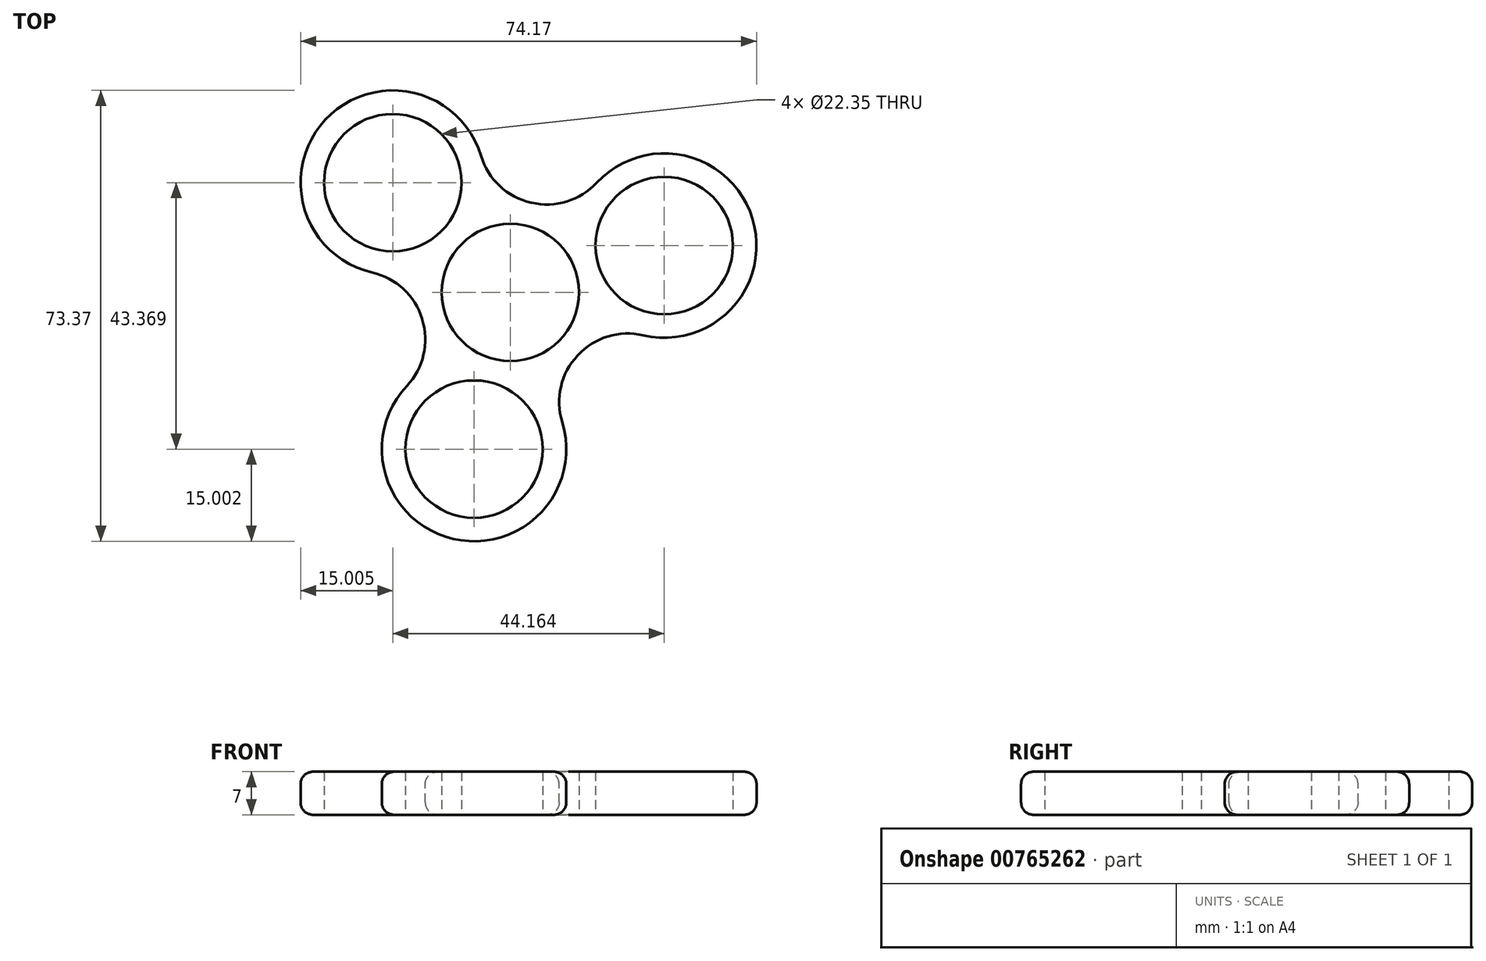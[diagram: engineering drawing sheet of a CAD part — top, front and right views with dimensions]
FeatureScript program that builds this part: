
annotation { "Feature Type Name" : "Feature", "Feature Type Description" : "" }
export const myFeature = defineFeature(function(context is Context, id is Id, definition is map)
    precondition{}
    {
        {
            var Q0;
            Q0=qCreatedBy(makeId("Top.planeOp"),FACE);
            var sketch = newSketch(context, id + "F0", { "sketchPlane" : qUnion([Q0])});
            skCircle(sketch, "E0", {"center": v(0, 0) * mm, "radius": 11.18 * mm});
            skLineSegment(sketch, "E1", {"start": v(0, 0) * mm, "end": v(-19.13, 17.87) * mm});
            skLineSegment(sketch, "E2", {"start": v(0, 0) * mm, "end": v(25.04, 7.63) * mm});
            skLineSegment(sketch, "E3", {"start": v(0, 0) * mm, "end": v(-5.91, -25.5) * mm});
            skCircle(sketch, "E4", {"center": v(-19.13, 17.87) * mm, "radius": 11.18 * mm});
            skCircle(sketch, "E5", {"center": v(25.04, 7.63) * mm, "radius": 11.18 * mm});
            skCircle(sketch, "E6", {"center": v(-5.91, -25.5) * mm, "radius": 11.18 * mm});
            skCircle(sketch, "E7", {"center": v(0, 0) * mm, "radius": 15 * mm});
            skCircle(sketch, "E8", {"center": v(-19.13, 17.87) * mm, "radius": 15 * mm});
            skCircle(sketch, "E9", {"center": v(25.04, 7.63) * mm, "radius": 15 * mm});
            skCircle(sketch, "E10", {"center": v(-5.91, -25.5) * mm, "radius": 15 * mm});
            skLineSegment(sketch, "E11", {"start": v(-19.13, 17.87) * mm, "end": v(-8.88, 28.83) * mm});
            skLineSegment(sketch, "E12", {"start": v(25.04, 7.63) * mm, "end": v(20.67, 21.98) * mm});
            skLineSegment(sketch, "E13", {"start": v(-5.91, -25.5) * mm, "end": v(8.7, -28.89) * mm});
            skLineSegment(sketch, "E14", {"start": v(-5.91, -25.5) * mm, "end": v(-20.53, -22.1) * mm});
            skLineSegment(sketch, "E15", {"start": v(-19.13, 17.87) * mm, "end": v(-29.37, 6.91) * mm});
            skLineSegment(sketch, "E16", {"start": v(25.04, 7.63) * mm, "end": v(29.41, -6.72) * mm});
            skArc(sketch, "E17", {"start": v(-8.88, 28.83) * mm, "mid": v(3.39, 14.61) * mm, "end": v(20.67, 21.98) * mm});
            skArc(sketch, "E18", {"start": v(-20.53, -22.1) * mm, "mid": v(-14.35, -4.37) * mm, "end": v(-29.37, 6.91) * mm});
            skArc(sketch, "E19", {"start": v(29.41, -6.72) * mm, "mid": v(10.96, -10.24) * mm, "end": v(8.7, -28.89) * mm});
            skSolve(sketch);
        }
        {
            var Q0;
            {var subQ0=sQuery(id+"F0.wireOp",EDGE,"E15");var subQ1=sQuery(id+"F0.wireOp",EDGE,"E4");var subQ2=makeQuery(id+"F0.imprint","INTERSECT",VERTEX,{"derivedFrom":[subQ1,subQ0]});Q0=makeQuery(id+"F0.imprint","IMPRINT",FACE,{"disambiguationData":[TD([[makeQuery(id+"F0.imprint","IMPRINT",EDGE,{"disambiguationData":[TD([[subQ2,1.0]])],"derivedFrom":subQ1}),-1.0]])]});}
            var Q1;
            {var subQ0=sQuery(id+"F0.wireOp",EDGE,"E17");var subQ1=sQuery(id+"F0.wireOp",EDGE,"E8");var subQ3=makeQuery(id+"F0.imprint","INTERSECT",VERTEX,{"derivedFrom":[subQ1,subQ0]});Q1=makeQuery(id+"F0.imprint","IMPRINT",FACE,{"disambiguationData":[TD([[makeQuery(id+"F0.imprint","IMPRINT",EDGE,{"disambiguationData":[TD([[subQ3,-1.0]])],"derivedFrom":subQ1}),1.0]])]});}
            var Q2;
            {var subQ0=sQuery(id+"F0.wireOp",EDGE,"E17");var subQ2=sQuery(id+"F0.wireOp",EDGE,"E8");var subQ6=makeQuery(id+"F0.imprint","INTERSECT",VERTEX,{"derivedFrom":[subQ2,subQ0]});Q2=makeQuery(id+"F0.imprint","IMPRINT",FACE,{"disambiguationData":[TD([[makeQuery(id+"F0.imprint","IMPRINT",EDGE,{"disambiguationData":[TD([[subQ6,1.0]])],"derivedFrom":subQ2}),1.0]])]});}
            var Q3;
            {var subQ0=sQuery(id+"F0.wireOp",EDGE,"E8");var subQ3=sQuery(id+"F0.wireOp",EDGE,"E7");var subQ5=makeQuery(id+"F0.imprint","INTERSECT",VERTEX,{"disambiguationData":[OD(0.0)],"derivedFrom":[subQ3,subQ0]});Q3=makeQuery(id+"F0.imprint","IMPRINT",FACE,{"disambiguationData":[TD([[makeQuery(id+"F0.imprint","IMPRINT",EDGE,{"disambiguationData":[TD([[subQ5,-1.0]])],"derivedFrom":subQ3}),1.0]])]});}
            var Q4;
            {var subQ0=sQuery(id+"F0.wireOp",EDGE,"E8");var subQ3=sQuery(id+"F0.wireOp",EDGE,"E7");var subQ5=makeQuery(id+"F0.imprint","INTERSECT",VERTEX,{"disambiguationData":[OD(1.0)],"derivedFrom":[subQ3,subQ0]});Q4=makeQuery(id+"F0.imprint","IMPRINT",FACE,{"disambiguationData":[TD([[makeQuery(id+"F0.imprint","IMPRINT",EDGE,{"disambiguationData":[TD([[subQ5,1.0]])],"derivedFrom":subQ3}),1.0]])]});}
            var Q5;
            {var subQ0=sQuery(id+"F0.wireOp",EDGE,"E18");var subQ1=sQuery(id+"F0.wireOp",EDGE,"E8");var subQ2=makeQuery(id+"F0.imprint","INTERSECT",VERTEX,{"derivedFrom":[subQ1,subQ0]});Q5=makeQuery(id+"F0.imprint","IMPRINT",FACE,{"disambiguationData":[TD([[makeQuery(id+"F0.imprint","IMPRINT",EDGE,{"disambiguationData":[TD([[subQ2,-1.0]])],"derivedFrom":subQ1}),1.0]])]});}
            var Q6;
            {var subQ0=sQuery(id+"F0.wireOp",EDGE,"E18");var subQ1=sQuery(id+"F0.wireOp",EDGE,"E8");var subQ3=makeQuery(id+"F0.imprint","INTERSECT",VERTEX,{"derivedFrom":[subQ1,subQ0]});Q6=makeQuery(id+"F0.imprint","IMPRINT",FACE,{"disambiguationData":[TD([[makeQuery(id+"F0.imprint","IMPRINT",EDGE,{"disambiguationData":[TD([[subQ3,1.0]])],"derivedFrom":subQ1}),1.0]])]});}
            var Q7;
            {var subQ0=sQuery(id+"F0.wireOp",EDGE,"E18");var subQ1=sQuery(id+"F0.wireOp",EDGE,"E10");var subQ3=makeQuery(id+"F0.imprint","INTERSECT",VERTEX,{"derivedFrom":[subQ1,subQ0]});Q7=makeQuery(id+"F0.imprint","IMPRINT",FACE,{"disambiguationData":[TD([[makeQuery(id+"F0.imprint","IMPRINT",EDGE,{"disambiguationData":[TD([[subQ3,-1.0]])],"derivedFrom":subQ1}),1.0]])]});}
            var Q8;
            {var subQ0=sQuery(id+"F0.wireOp",EDGE,"E18");var subQ2=sQuery(id+"F0.wireOp",EDGE,"E10");var subQ6=makeQuery(id+"F0.imprint","INTERSECT",VERTEX,{"derivedFrom":[subQ2,subQ0]});Q8=makeQuery(id+"F0.imprint","IMPRINT",FACE,{"disambiguationData":[TD([[makeQuery(id+"F0.imprint","IMPRINT",EDGE,{"disambiguationData":[TD([[subQ6,1.0]])],"derivedFrom":subQ2}),1.0]])]});}
            var Q9;
            {var subQ0=sQuery(id+"F0.wireOp",EDGE,"E10");var subQ3=sQuery(id+"F0.wireOp",EDGE,"E7");var subQ5=makeQuery(id+"F0.imprint","INTERSECT",VERTEX,{"disambiguationData":[OD(0.0)],"derivedFrom":[subQ3,subQ0]});Q9=makeQuery(id+"F0.imprint","IMPRINT",FACE,{"disambiguationData":[TD([[makeQuery(id+"F0.imprint","IMPRINT",EDGE,{"disambiguationData":[TD([[subQ5,-1.0]])],"derivedFrom":subQ3}),1.0]])]});}
            var Q10;
            {var subQ0=sQuery(id+"F0.wireOp",EDGE,"E10");var subQ3=sQuery(id+"F0.wireOp",EDGE,"E7");var subQ5=makeQuery(id+"F0.imprint","INTERSECT",VERTEX,{"disambiguationData":[OD(1.0)],"derivedFrom":[subQ3,subQ0]});Q10=makeQuery(id+"F0.imprint","IMPRINT",FACE,{"disambiguationData":[TD([[makeQuery(id+"F0.imprint","IMPRINT",EDGE,{"disambiguationData":[TD([[subQ5,1.0]])],"derivedFrom":subQ3}),1.0]])]});}
            var Q11;
            {var subQ0=sQuery(id+"F0.wireOp",EDGE,"E19");var subQ1=sQuery(id+"F0.wireOp",EDGE,"E10");var subQ3=makeQuery(id+"F0.imprint","INTERSECT",VERTEX,{"derivedFrom":[subQ1,subQ0]});Q11=makeQuery(id+"F0.imprint","IMPRINT",FACE,{"disambiguationData":[TD([[makeQuery(id+"F0.imprint","IMPRINT",EDGE,{"disambiguationData":[TD([[subQ3,1.0]])],"derivedFrom":subQ1}),1.0]])]});}
            var Q12;
            {var subQ0=sQuery(id+"F0.wireOp",EDGE,"E19");var subQ1=sQuery(id+"F0.wireOp",EDGE,"E10");var subQ2=makeQuery(id+"F0.imprint","INTERSECT",VERTEX,{"derivedFrom":[subQ1,subQ0]});Q12=makeQuery(id+"F0.imprint","IMPRINT",FACE,{"disambiguationData":[TD([[makeQuery(id+"F0.imprint","IMPRINT",EDGE,{"disambiguationData":[TD([[subQ2,-1.0]])],"derivedFrom":subQ1}),1.0]])]});}
            var Q13;
            {var subQ0=sQuery(id+"F0.wireOp",EDGE,"E14");var subQ1=sQuery(id+"F0.wireOp",EDGE,"E6");var subQ2=makeQuery(id+"F0.imprint","INTERSECT",VERTEX,{"derivedFrom":[subQ1,subQ0]});Q13=makeQuery(id+"F0.imprint","IMPRINT",FACE,{"disambiguationData":[TD([[makeQuery(id+"F0.imprint","IMPRINT",EDGE,{"disambiguationData":[TD([[subQ2,-1.0]])],"derivedFrom":subQ1}),-1.0]])]});}
            var Q14;
            {var subQ1=sQuery(id+"F0.wireOp",EDGE,"E7");var subQ5=makeQuery(id+"F0.imprint","INTERSECT",VERTEX,{"derivedFrom":[subQ1,sQuery(id+"F0.wireOp",EDGE,"E18")]});Q14=makeQuery(id+"F0.imprint","IMPRINT",FACE,{"disambiguationData":[TD([[makeQuery(id+"F0.imprint","IMPRINT",EDGE,{"disambiguationData":[TD([[subQ5,1.0]])],"derivedFrom":subQ1}),1.0]])]});}
            var Q15;
            {var subQ1=sQuery(id+"F0.wireOp",EDGE,"E7");var subQ5=makeQuery(id+"F0.imprint","INTERSECT",VERTEX,{"derivedFrom":[subQ1,sQuery(id+"F0.wireOp",EDGE,"E19")]});Q15=makeQuery(id+"F0.imprint","IMPRINT",FACE,{"disambiguationData":[TD([[makeQuery(id+"F0.imprint","IMPRINT",EDGE,{"disambiguationData":[TD([[subQ5,1.0]])],"derivedFrom":subQ1}),1.0]])]});}
            var Q16;
            {var subQ0=sQuery(id+"F0.wireOp",EDGE,"E9");var subQ3=sQuery(id+"F0.wireOp",EDGE,"E7");var subQ5=makeQuery(id+"F0.imprint","INTERSECT",VERTEX,{"disambiguationData":[OD(1.0)],"derivedFrom":[subQ3,subQ0]});Q16=makeQuery(id+"F0.imprint","IMPRINT",FACE,{"disambiguationData":[TD([[makeQuery(id+"F0.imprint","IMPRINT",EDGE,{"disambiguationData":[TD([[subQ5,-1.0]])],"derivedFrom":subQ3}),1.0]])]});}
            var Q17;
            {var subQ0=sQuery(id+"F0.wireOp",EDGE,"E9");var subQ3=sQuery(id+"F0.wireOp",EDGE,"E7");var subQ5=makeQuery(id+"F0.imprint","INTERSECT",VERTEX,{"disambiguationData":[OD(0.0)],"derivedFrom":[subQ3,subQ0]});Q17=makeQuery(id+"F0.imprint","IMPRINT",FACE,{"disambiguationData":[TD([[makeQuery(id+"F0.imprint","IMPRINT",EDGE,{"disambiguationData":[TD([[subQ5,1.0]])],"derivedFrom":subQ3}),1.0]])]});}
            var Q18;
            {var subQ1=sQuery(id+"F0.wireOp",EDGE,"E7");var subQ5=makeQuery(id+"F0.imprint","INTERSECT",VERTEX,{"derivedFrom":[subQ1,sQuery(id+"F0.wireOp",EDGE,"E17")]});Q18=makeQuery(id+"F0.imprint","IMPRINT",FACE,{"disambiguationData":[TD([[makeQuery(id+"F0.imprint","IMPRINT",EDGE,{"disambiguationData":[TD([[subQ5,1.0]])],"derivedFrom":subQ1}),1.0]])]});}
            var Q19;
            {var subQ0=sQuery(id+"F0.wireOp",EDGE,"E17");var subQ2=sQuery(id+"F0.wireOp",EDGE,"E9");var subQ6=makeQuery(id+"F0.imprint","INTERSECT",VERTEX,{"derivedFrom":[subQ2,subQ0]});Q19=makeQuery(id+"F0.imprint","IMPRINT",FACE,{"disambiguationData":[TD([[makeQuery(id+"F0.imprint","IMPRINT",EDGE,{"disambiguationData":[TD([[subQ6,-1.0]])],"derivedFrom":subQ2}),1.0]])]});}
            var Q20;
            {var subQ0=sQuery(id+"F0.wireOp",EDGE,"E17");var subQ1=sQuery(id+"F0.wireOp",EDGE,"E9");var subQ3=makeQuery(id+"F0.imprint","INTERSECT",VERTEX,{"derivedFrom":[subQ1,subQ0]});Q20=makeQuery(id+"F0.imprint","IMPRINT",FACE,{"disambiguationData":[TD([[makeQuery(id+"F0.imprint","IMPRINT",EDGE,{"disambiguationData":[TD([[subQ3,1.0]])],"derivedFrom":subQ1}),1.0]])]});}
            var Q21;
            {var subQ0=sQuery(id+"F0.wireOp",EDGE,"E12");var subQ1=sQuery(id+"F0.wireOp",EDGE,"E5");var subQ2=makeQuery(id+"F0.imprint","INTERSECT",VERTEX,{"derivedFrom":[subQ1,subQ0]});Q21=makeQuery(id+"F0.imprint","IMPRINT",FACE,{"disambiguationData":[TD([[makeQuery(id+"F0.imprint","IMPRINT",EDGE,{"disambiguationData":[TD([[subQ2,1.0]])],"derivedFrom":subQ1}),-1.0]])]});}
            var Q22;
            {var subQ0=sQuery(id+"F0.wireOp",EDGE,"E19");var subQ2=sQuery(id+"F0.wireOp",EDGE,"E9");var subQ9=makeQuery(id+"F0.imprint","INTERSECT",VERTEX,{"derivedFrom":[subQ2,subQ0]});Q22=makeQuery(id+"F0.imprint","IMPRINT",FACE,{"disambiguationData":[TD([[makeQuery(id+"F0.imprint","IMPRINT",EDGE,{"disambiguationData":[TD([[subQ9,1.0]])],"derivedFrom":subQ2}),1.0]])]});}
            var Q23;
            {var subQ0=sQuery(id+"F0.wireOp",EDGE,"E19");var subQ1=sQuery(id+"F0.wireOp",EDGE,"E9");var subQ3=makeQuery(id+"F0.imprint","INTERSECT",VERTEX,{"derivedFrom":[subQ1,subQ0]});Q23=makeQuery(id+"F0.imprint","IMPRINT",FACE,{"disambiguationData":[TD([[makeQuery(id+"F0.imprint","IMPRINT",EDGE,{"disambiguationData":[TD([[subQ3,-1.0]])],"derivedFrom":subQ1}),1.0]])]});}
            extrude(context, id + "F1", {"entities" : qUnion([Q0, Q1, Q2, Q3, Q4, Q5, Q6, Q7, Q8, Q9, Q10, Q11, Q12, Q13, Q14, Q15, Q16, Q17, Q18, Q19, Q20, Q21, Q22, Q23]), "depth" : 7 * mm, "offsetDistance" : 25 * mm});
        }
        {
            var Q0;
            {var subQ0=sQuery(id+"F0.wireOp",EDGE,"E8");var subQ1=sQuery(id+"F0.wireOp",EDGE,"E7");Q0=makeQuery(id+"F1.opExtrude","SWEPT_EDGE",EDGE,{"disambiguationData":[OSD([subQ1,subQ0]),TDD([makeQuery(id+"F0.imprint","INTERSECT",VERTEX,{"disambiguationData":[OD(1.0)],"derivedFrom":[subQ1,subQ0]})])]});}
            var Q1;
            {var subQ0=sQuery(id+"F0.wireOp",EDGE,"E10");var subQ1=sQuery(id+"F0.wireOp",EDGE,"E7");Q1=makeQuery(id+"F1.opExtrude","SWEPT_EDGE",EDGE,{"disambiguationData":[OSD([subQ1,subQ0]),TDD([makeQuery(id+"F0.imprint","INTERSECT",VERTEX,{"disambiguationData":[OD(0.0)],"derivedFrom":[subQ1,subQ0]})])]});}
            var Q2;
            {var subQ0=sQuery(id+"F0.wireOp",EDGE,"E9");var subQ1=sQuery(id+"F0.wireOp",EDGE,"E7");Q2=makeQuery(id+"F1.opExtrude","SWEPT_EDGE",EDGE,{"disambiguationData":[OSD([subQ1,subQ0]),TDD([makeQuery(id+"F0.imprint","INTERSECT",VERTEX,{"disambiguationData":[OD(0.0)],"derivedFrom":[subQ1,subQ0]})])]});}
            var Q3;
            {var subQ0=sQuery(id+"F0.wireOp",EDGE,"E8");var subQ1=sQuery(id+"F0.wireOp",EDGE,"E7");Q3=makeQuery(id+"F1.opExtrude","SWEPT_EDGE",EDGE,{"disambiguationData":[OSD([subQ1,subQ0]),TDD([makeQuery(id+"F0.imprint","INTERSECT",VERTEX,{"disambiguationData":[OD(0.0)],"derivedFrom":[subQ1,subQ0]})])]});}
            var Q4;
            {var subQ0=sQuery(id+"F0.wireOp",EDGE,"E9");var subQ1=sQuery(id+"F0.wireOp",EDGE,"E7");Q4=makeQuery(id+"F1.opExtrude","SWEPT_EDGE",EDGE,{"disambiguationData":[OSD([subQ1,subQ0]),TDD([makeQuery(id+"F0.imprint","INTERSECT",VERTEX,{"disambiguationData":[OD(1.0)],"derivedFrom":[subQ1,subQ0]})])]});}
            var Q5;
            {var subQ0=sQuery(id+"F0.wireOp",EDGE,"E10");var subQ1=sQuery(id+"F0.wireOp",EDGE,"E7");Q5=makeQuery(id+"F1.opExtrude","SWEPT_EDGE",EDGE,{"disambiguationData":[OSD([subQ1,subQ0]),TDD([makeQuery(id+"F0.imprint","INTERSECT",VERTEX,{"disambiguationData":[OD(1.0)],"derivedFrom":[subQ1,subQ0]})])]});}
            fillet(context, id + "F2", {"entities" : qUnion([Q0, Q1, Q2, Q3, Q4, Q5]), "radius" : 11.05 * mm, "tangentPropagation" : true, "allowEdgeOverflow" : false});
        }
        {
            var Q0;
            Q0=makeQuery(id+"F1.opExtrude","CAP_EDGE",EDGE,{"disambiguationData":[OSD([sQuery(id+"F0.wireOp",EDGE,"E8")])],"isStart":false});
            var Q1;
            Q1=makeQuery(id+"F1.opExtrude","CAP_EDGE",EDGE,{"disambiguationData":[OSD([sQuery(id+"F0.wireOp",EDGE,"E8")])],"isStart":true});
            fillet(context, id + "F3", {"entities" : qUnion([Q0, Q1]), "radius" : 2 * mm, "tangentPropagation" : true, "allowEdgeOverflow" : false});
        }
    });
